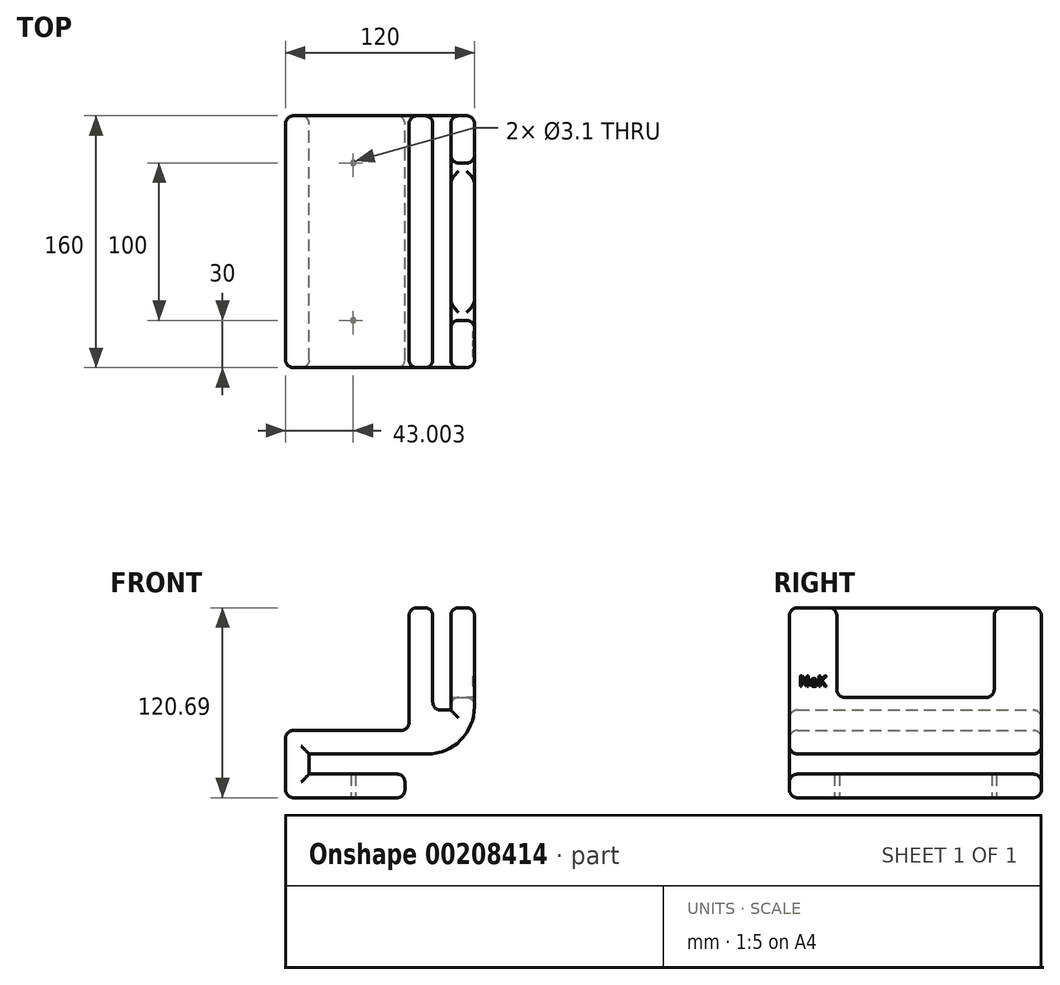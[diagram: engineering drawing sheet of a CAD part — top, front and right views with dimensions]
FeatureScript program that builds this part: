
annotation { "Feature Type Name" : "Feature", "Feature Type Description" : "" }
export const myFeature = defineFeature(function(context is Context, id is Id, definition is map)
    precondition{}
    {
        {
            var Q0;
            Q0=qCreatedBy(makeId("Front.planeOp"),FACE);
            var sketch = newSketch(context, id + "F0", { "sketchPlane" : qUnion([Q0])});
            skLineSegment(sketch, "E0", {"start": v(94.94, 65) * mm, "end": v(94.94, 0) * mm});
            skLineSegment(sketch, "E1", {"start": v(94.94, 65) * mm, "end": v(79.94, 65) * mm});
            skLineSegment(sketch, "E2", {"start": v(79.94, 0) * mm, "end": v(79.94, 65) * mm});
            skLineSegment(sketch, "E3", {"start": v(79.94, 0) * mm, "end": v(68.44, 0) * mm});
            skLineSegment(sketch, "E4", {"start": v(68.44, 0) * mm, "end": v(68.44, 65) * mm});
            skLineSegment(sketch, "E5", {"start": v(68.44, 65) * mm, "end": v(53.44, 65) * mm});
            skLineSegment(sketch, "E6", {"start": v(53.44, 65) * mm, "end": v(53.44, 0) * mm});
            skLineSegment(sketch, "E7", {"start": v(53.44, 0) * mm, "end": v(53.44, -12.89) * mm});
            skLineSegment(sketch, "E8", {"start": v(53.44, -12.89) * mm, "end": v(-25.06, -12.89) * mm});
            skLineSegment(sketch, "E9", {"start": v(-25.06, -12.89) * mm, "end": v(-25.06, -55.69) * mm});
            skLineSegment(sketch, "E10", {"start": v(-25.06, -55.69) * mm, "end": v(61.57, -55.69) * mm});
            skLineSegment(sketch, "E11", {"start": v(94.94, 0) * mm, "end": v(94.94, -27.89) * mm});
            skLineSegment(sketch, "E12", {"start": v(94.94, -27.89) * mm, "end": v(-10.06, -27.89) * mm});
            skLineSegment(sketch, "E13", {"start": v(-10.06, -27.89) * mm, "end": v(-10.06, -40.69) * mm});
            skLineSegment(sketch, "E14", {"start": v(-10.06, -40.69) * mm, "end": v(50.76, -40.69) * mm});
            skLineSegment(sketch, "E15", {"start": v(50.76, -40.69) * mm, "end": v(50.76, -55.69) * mm});
            skLineSegment(sketch, "E16.bottom", {"start": v(79.94, 65) * mm, "end": v(94.94, 65) * mm});
            skLineSegment(sketch, "E16.top", {"start": v(79.94, 8) * mm, "end": v(94.94, 8) * mm});
            skLineSegment(sketch, "E16.left", {"start": v(79.94, 65) * mm, "end": v(79.94, 8) * mm});
            skLineSegment(sketch, "E16.right", {"start": v(94.94, 65) * mm, "end": v(94.94, 8) * mm});
            skSolve(sketch);
        }
        {
            var Q0;
            {var subQ7=sQuery(id+"F0.wireOp",EDGE,"E3");Q0=makeQuery(id+"F0.imprint","IMPRINT",FACE,{"disambiguationData":[TD([[makeQuery(id+"F0.imprint","IMPRINT",EDGE,{"derivedFrom":subQ7}),1.0]])]});}
            var Q1;
            {var subQ0=sQuery(id+"F0.wireOp",EDGE,"E1");Q1=makeQuery(id+"F0.imprint","IMPRINT",FACE,{"disambiguationData":[TD([[makeQuery(id+"F0.imprint","IMPRINT",EDGE,{"derivedFrom":subQ0}),1.0]])]});}
            extrude(context, id + "F1", {"entities" : qUnion([Q0, Q1]), "depth" : 80 * mm, "hasSecondDirection" : true, "secondDirectionOppositeDirection" : true, "secondDirectionDepth" : 80 * mm});
        }
        {
            var Q0;
            {var subQ0=sQuery(id+"F0.wireOp",EDGE,"E1");Q0=makeQuery(id+"F0.imprint","IMPRINT",FACE,{"disambiguationData":[TD([[makeQuery(id+"F0.imprint","IMPRINT",EDGE,{"derivedFrom":subQ0}),1.0]])]});}
            extrude(context, id + "F2", {"entities" : qUnion([Q0]), "operationType" : NewBodyOperationType.REMOVE, "depth" : 50 * mm, "hasSecondDirection" : true, "secondDirectionOppositeDirection" : true, "secondDirectionDepth" : 50 * mm});
        }
        {
            var Q0;
            Q0=makeQuery(id+"F1.opExtrude","CAP_FACE",FACE,{"disambiguationData":[OSD([sQuery(id+"F0.wireOp",EDGE,"E0"),sQuery(id+"F0.wireOp",EDGE,"E1"),sQuery(id+"F0.wireOp",EDGE,"E2"),sQuery(id+"F0.wireOp",EDGE,"E3"),sQuery(id+"F0.wireOp",EDGE,"E4"),sQuery(id+"F0.wireOp",EDGE,"E5"),sQuery(id+"F0.wireOp",EDGE,"E6"),sQuery(id+"F0.wireOp",EDGE,"E7"),sQuery(id+"F0.wireOp",EDGE,"E8"),sQuery(id+"F0.wireOp",EDGE,"E9"),sQuery(id+"F0.wireOp",EDGE,"E10"),sQuery(id+"F0.wireOp",EDGE,"E11"),sQuery(id+"F0.wireOp",EDGE,"E12"),sQuery(id+"F0.wireOp",EDGE,"E13"),sQuery(id+"F0.wireOp",EDGE,"E14"),sQuery(id+"F0.wireOp",EDGE,"E15")])],"isStart":false});
            var Q1;
            Q1=makeQuery(id+"F1.opExtrude","CAP_FACE",FACE,{"disambiguationData":[OSD([sQuery(id+"F0.wireOp",EDGE,"E0"),sQuery(id+"F0.wireOp",EDGE,"E1"),sQuery(id+"F0.wireOp",EDGE,"E2"),sQuery(id+"F0.wireOp",EDGE,"E3"),sQuery(id+"F0.wireOp",EDGE,"E4"),sQuery(id+"F0.wireOp",EDGE,"E5"),sQuery(id+"F0.wireOp",EDGE,"E6"),sQuery(id+"F0.wireOp",EDGE,"E7"),sQuery(id+"F0.wireOp",EDGE,"E8"),sQuery(id+"F0.wireOp",EDGE,"E9"),sQuery(id+"F0.wireOp",EDGE,"E10"),sQuery(id+"F0.wireOp",EDGE,"E11"),sQuery(id+"F0.wireOp",EDGE,"E12"),sQuery(id+"F0.wireOp",EDGE,"E13"),sQuery(id+"F0.wireOp",EDGE,"E14"),sQuery(id+"F0.wireOp",EDGE,"E15")])],"isStart":true});
            var Q2;
            Q2=makeQuery(id+"F1.opExtrude","SWEPT_FACE",FACE,{"disambiguationData":[OSD([sQuery(id+"F0.wireOp",EDGE,"E15")])]});
            var Q3;
            Q3=makeQuery(id+"F1.opExtrude","SWEPT_FACE",FACE,{"disambiguationData":[OSD([sQuery(id+"F0.wireOp",EDGE,"E9")])]});
            var Q4;
            Q4=makeQuery(id+"F1.opExtrude","SWEPT_FACE",FACE,{"disambiguationData":[OSD([sQuery(id+"F0.wireOp",EDGE,"E6"),sQuery(id+"F0.wireOp",EDGE,"E7")])]});
            var Q5;
            Q5=makeQuery(id+"F1.opExtrude","SWEPT_FACE",FACE,{"disambiguationData":[OSD([sQuery(id+"F0.wireOp",EDGE,"E4")])]});
            var Q6;
            Q6=makeQuery(id+"F2.boolean.opBoolean","COPY",FACE,{"derivedFrom":makeQuery(id+"F2.opExtrude","CAP_FACE",FACE,{"disambiguationData":[OSD([sQuery(id+"F0.wireOp",EDGE,"E0"),sQuery(id+"F0.wireOp",EDGE,"E1"),sQuery(id+"F0.wireOp",EDGE,"E2"),sQuery(id+"F0.wireOp",EDGE,"E16.top")])],"isStart":false})});
            var Q7;
            Q7=makeQuery(id+"F2.boolean.opBoolean","COPY",FACE,{"derivedFrom":makeQuery(id+"F2.opExtrude","CAP_FACE",FACE,{"disambiguationData":[OSD([sQuery(id+"F0.wireOp",EDGE,"E0"),sQuery(id+"F0.wireOp",EDGE,"E1"),sQuery(id+"F0.wireOp",EDGE,"E2"),sQuery(id+"F0.wireOp",EDGE,"E16.top")])],"isStart":true})});
            var Q8;
            {var subQ0=sQuery(id+"F0.wireOp",EDGE,"E2");var subQ1=sQuery(id+"F0.wireOp",EDGE,"E1");var subQ2=sQuery(id+"F0.wireOp",EDGE,"E0");Q8=makeQuery(id+"F2.boolean.opBoolean","SPLIT",EDGE,{"disambiguationData":[TD([makeQuery(id+"F2.opExtrude","CAP_FACE",FACE,{"disambiguationData":[OSD([subQ2,subQ1,subQ0,sQuery(id+"F0.wireOp",EDGE,"E16.top")])],"isStart":true})])],"derivedFrom":makeQuery(id+"F1.opExtrude","SWEPT_EDGE",EDGE,{"disambiguationData":[OSD([subQ1,subQ0])]})});}
            var Q9;
            {var subQ0=sQuery(id+"F0.wireOp",EDGE,"E2");var subQ1=sQuery(id+"F0.wireOp",EDGE,"E1");var subQ2=sQuery(id+"F0.wireOp",EDGE,"E0");Q9=makeQuery(id+"F2.boolean.opBoolean","SPLIT",EDGE,{"disambiguationData":[TD([makeQuery(id+"F2.opExtrude","CAP_FACE",FACE,{"disambiguationData":[OSD([subQ2,subQ1,subQ0,sQuery(id+"F0.wireOp",EDGE,"E16.top")])],"isStart":false})])],"derivedFrom":makeQuery(id+"F1.opExtrude","SWEPT_EDGE",EDGE,{"disambiguationData":[OSD([subQ1,subQ0])]})});}
            var Q10;
            {var subQ1=sQuery(id+"F0.wireOp",EDGE,"E2");var subQ2=sQuery(id+"F0.wireOp",EDGE,"E1");var subQ3=sQuery(id+"F0.wireOp",EDGE,"E0");Q10=makeQuery(id+"F2.boolean.opBoolean","SPLIT",EDGE,{"disambiguationData":[TD([makeQuery(id+"F2.opExtrude","CAP_FACE",FACE,{"disambiguationData":[OSD([subQ3,subQ2,subQ1,sQuery(id+"F0.wireOp",EDGE,"E16.top")])],"isStart":false})])],"derivedFrom":makeQuery(id+"F1.opExtrude","SWEPT_EDGE",EDGE,{"disambiguationData":[OSD([subQ3,subQ2])]})});}
            var Q11;
            {var subQ1=sQuery(id+"F0.wireOp",EDGE,"E2");var subQ2=sQuery(id+"F0.wireOp",EDGE,"E1");var subQ3=sQuery(id+"F0.wireOp",EDGE,"E0");Q11=makeQuery(id+"F2.boolean.opBoolean","SPLIT",EDGE,{"disambiguationData":[TD([makeQuery(id+"F2.opExtrude","CAP_FACE",FACE,{"disambiguationData":[OSD([subQ3,subQ2,subQ1,sQuery(id+"F0.wireOp",EDGE,"E16.top")])],"isStart":true})])],"derivedFrom":makeQuery(id+"F1.opExtrude","SWEPT_EDGE",EDGE,{"disambiguationData":[OSD([subQ3,subQ2])]})});}
            fillet(context, id + "F3", {"entities" : qUnion([Q0, Q1, Q2, Q3, Q4, Q5, Q6, Q7, Q8, Q9, Q10, Q11]), "radius" : 5 * mm, "tangentPropagation" : true, "allowEdgeOverflow" : false});
        }
        {
            var Q0;
            Q0=makeQuery(id+"F1.opExtrude","SWEPT_EDGE",EDGE,{"disambiguationData":[OSD([sQuery(id+"F0.wireOp",EDGE,"E11"),sQuery(id+"F0.wireOp",EDGE,"E12")])]});
            fillet(context, id + "F4", {"entities" : qUnion([Q0]), "radius" : 30 * mm, "tangentPropagation" : true, "allowEdgeOverflow" : false});
        }
        {
            var Q0;
            Q0=makeQuery(id+"F1.opExtrude","SWEPT_FACE",FACE,{"disambiguationData":[OSD([sQuery(id+"F0.wireOp",EDGE,"E10")])]});
            var sketch = newSketch(context, id + "F5", { "sketchPlane" : qUnion([Q0])});
            skPoint(sketch, "E17", {"position": v(17.94, -50) * mm});
            skPoint(sketch, "E18", {"position": v(17.94, 50) * mm});
            skCircle(sketch, "E19", {"center": v(17.94, -50) * mm, "radius": 1.55 * mm});
            skCircle(sketch, "E20", {"center": v(17.94, 50) * mm, "radius": 1.55 * mm});
            skSolve(sketch);
        }
        {
            var Q0;
            Q0=makeQuery(id+"F5.imprint","IMPRINT",FACE,{"disambiguationData":[TD([[makeQuery(id+"F5.imprint","IMPRINT",EDGE,{"derivedFrom":sQuery(id+"F5.wireOp",EDGE,"E19")}),1.0]])]});
            var Q1;
            Q1=makeQuery(id+"F5.imprint","IMPRINT",FACE,{"disambiguationData":[TD([[makeQuery(id+"F5.imprint","IMPRINT",EDGE,{"derivedFrom":sQuery(id+"F5.wireOp",EDGE,"E20")}),1.0]])]});
            extrude(context, id + "F6", {"entities" : qUnion([Q0, Q1]), "operationType" : NewBodyOperationType.REMOVE, "oppositeDirection" : true, "depth" : 25 * mm});
        }
        {
            var Q0;
            Q0=makeQuery(id+"F1.opExtrude","SWEPT_FACE",FACE,{"disambiguationData":[OSD([sQuery(id+"F0.wireOp",EDGE,"E0"),sQuery(id+"F0.wireOp",EDGE,"E11")])]});
            var sketch = newSketch(context, id + "F7", { "sketchPlane" : qUnion([Q0])});
            skText(sketch, "E21", { "text": "NeK", "fontName": "OpenSans-Regular.ttf"});
            const initialGuessF7  = {"E21": [-0.074, 0.01512, 1, 0, 0.0065]};
            skSetInitialGuess(sketch, initialGuessF7);
            skSolve(sketch);
        }
        {
            var Q0;
            Q0 = qSketchRegion(id + "F7", true);
            extrude(context, id + "F8", {"entities" : qUnion([Q0]), "operationType" : NewBodyOperationType.REMOVE, "oppositeDirection" : true, "offsetDistance" : 25 * mm, "depth" : 1 * mm});
        }
        {
            var Q0;
            Q0=makeQuery(id+"F8.boolean.opBoolean","COPY",FACE,{"derivedFrom":makeQuery(id+"F8.opExtrude","CAP_FACE",FACE,{"disambiguationData":[OSD([sQuery(id+"F7.wireOp",EDGE,"E21.sketch_text.stroke-0"),sQuery(id+"F7.wireOp",EDGE,"E21.sketch_text.stroke-1"),sQuery(id+"F7.wireOp",EDGE,"E21.sketch_text.stroke-2"),sQuery(id+"F7.wireOp",EDGE,"E21.sketch_text.stroke-3"),sQuery(id+"F7.wireOp",EDGE,"E21.sketch_text.stroke-4"),sQuery(id+"F7.wireOp",EDGE,"E21.sketch_text.stroke-5"),sQuery(id+"F7.wireOp",EDGE,"E21.sketch_text.stroke-6"),sQuery(id+"F7.wireOp",EDGE,"E21.sketch_text.stroke-7"),sQuery(id+"F7.wireOp",EDGE,"E21.sketch_text.stroke-8"),sQuery(id+"F7.wireOp",EDGE,"E21.sketch_text.stroke-9"),sQuery(id+"F7.wireOp",EDGE,"E21.sketch_text.stroke-10"),sQuery(id+"F7.wireOp",EDGE,"E21.sketch_text.stroke-11"),sQuery(id+"F7.wireOp",EDGE,"E21.sketch_text.stroke-12"),sQuery(id+"F7.wireOp",EDGE,"E21.sketch_text.stroke-13"),sQuery(id+"F7.wireOp",EDGE,"E21.sketch_text.stroke-14")])],"isStart":false})});
            var Q1;
            Q1=makeQuery(id+"F8.boolean.opBoolean","COPY",FACE,{"derivedFrom":makeQuery(id+"F8.opExtrude","CAP_FACE",FACE,{"disambiguationData":[OSD([sQuery(id+"F7.wireOp",EDGE,"E21.sketch_text.stroke-15"),sQuery(id+"F7.wireOp",EDGE,"E21.sketch_text.stroke-16"),sQuery(id+"F7.wireOp",EDGE,"E21.sketch_text.stroke-17"),sQuery(id+"F7.wireOp",EDGE,"E21.sketch_text.stroke-18"),sQuery(id+"F7.wireOp",EDGE,"E21.sketch_text.stroke-19"),sQuery(id+"F7.wireOp",EDGE,"E21.sketch_text.stroke-20"),sQuery(id+"F7.wireOp",EDGE,"E21.sketch_text.stroke-21"),sQuery(id+"F7.wireOp",EDGE,"E21.sketch_text.stroke-22"),sQuery(id+"F7.wireOp",EDGE,"E21.sketch_text.stroke-23"),sQuery(id+"F7.wireOp",EDGE,"E21.sketch_text.stroke-24"),sQuery(id+"F7.wireOp",EDGE,"E21.sketch_text.stroke-25"),sQuery(id+"F7.wireOp",EDGE,"E21.sketch_text.stroke-26"),sQuery(id+"F7.wireOp",EDGE,"E21.sketch_text.stroke-27"),sQuery(id+"F7.wireOp",EDGE,"E21.sketch_text.stroke-28"),sQuery(id+"F7.wireOp",EDGE,"E21.sketch_text.stroke-29"),sQuery(id+"F7.wireOp",EDGE,"E21.sketch_text.stroke-30"),sQuery(id+"F7.wireOp",EDGE,"E21.sketch_text.stroke-31"),sQuery(id+"F7.wireOp",EDGE,"E21.sketch_text.stroke-32"),sQuery(id+"F7.wireOp",EDGE,"E21.sketch_text.stroke-33")])],"isStart":false})});
            var Q2;
            Q2=makeQuery(id+"F8.boolean.opBoolean","COPY",FACE,{"derivedFrom":makeQuery(id+"F8.opExtrude","CAP_FACE",FACE,{"disambiguationData":[OSD([sQuery(id+"F7.wireOp",EDGE,"E21.sketch_text.stroke-34"),sQuery(id+"F7.wireOp",EDGE,"E21.sketch_text.stroke-35"),sQuery(id+"F7.wireOp",EDGE,"E21.sketch_text.stroke-36"),sQuery(id+"F7.wireOp",EDGE,"E21.sketch_text.stroke-37"),sQuery(id+"F7.wireOp",EDGE,"E21.sketch_text.stroke-38"),sQuery(id+"F7.wireOp",EDGE,"E21.sketch_text.stroke-39"),sQuery(id+"F7.wireOp",EDGE,"E21.sketch_text.stroke-40"),sQuery(id+"F7.wireOp",EDGE,"E21.sketch_text.stroke-41"),sQuery(id+"F7.wireOp",EDGE,"E21.sketch_text.stroke-42"),sQuery(id+"F7.wireOp",EDGE,"E21.sketch_text.stroke-43"),sQuery(id+"F7.wireOp",EDGE,"E21.sketch_text.stroke-44"),sQuery(id+"F7.wireOp",EDGE,"E21.sketch_text.stroke-45")])],"isStart":false})});
            fillet(context, id + "F9", {"entities" : qUnion([Q0, Q1, Q2]), "radius" : 0.2 * mm, "tangentPropagation" : true, "allowEdgeOverflow" : false});
        }
    });
